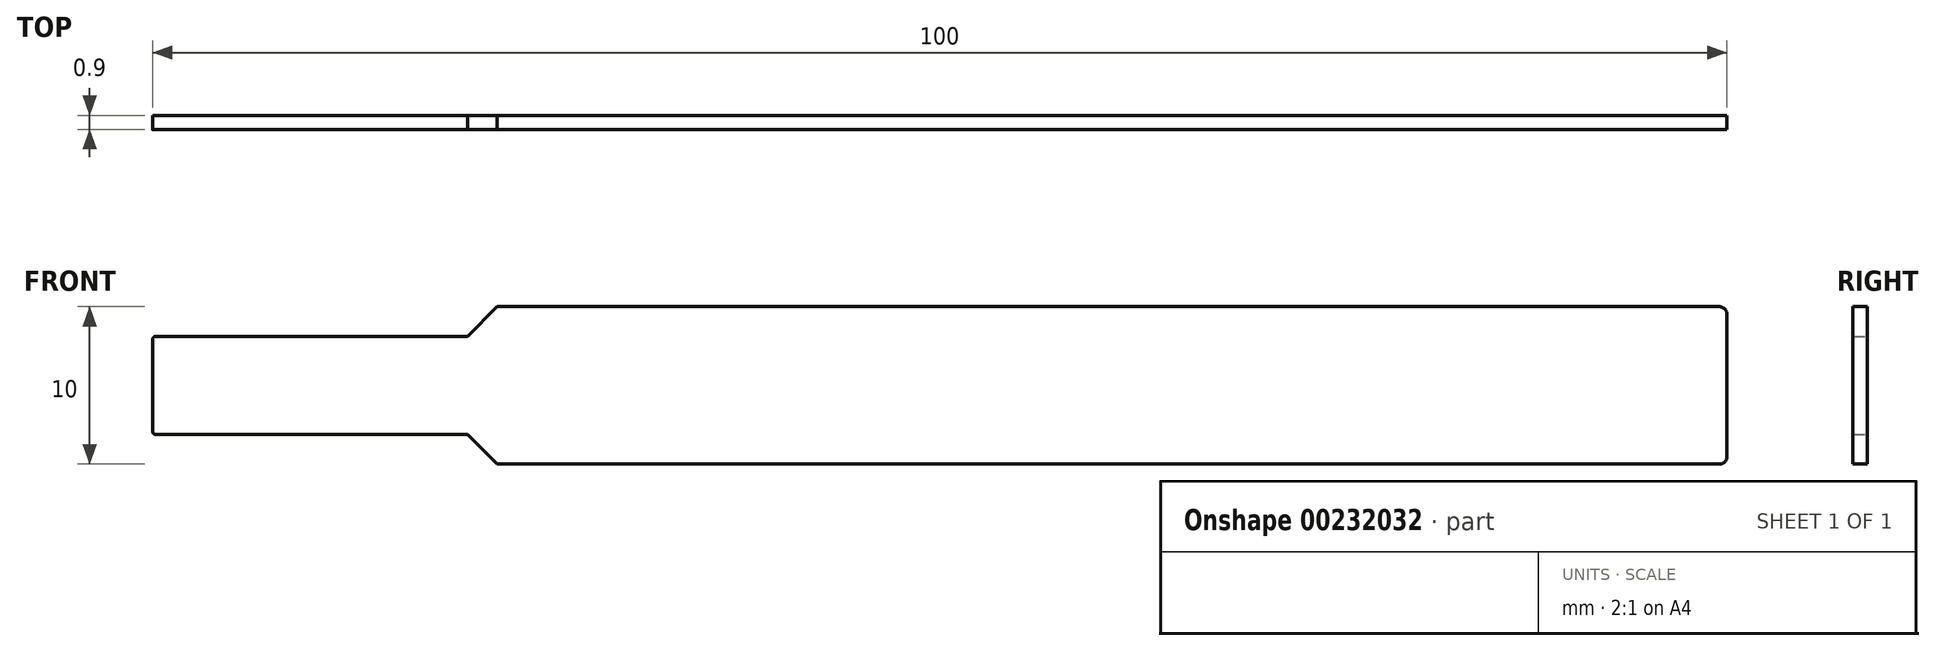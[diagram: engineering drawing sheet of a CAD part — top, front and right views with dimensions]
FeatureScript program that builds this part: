
annotation { "Feature Type Name" : "Feature", "Feature Type Description" : "" }
export const myFeature = defineFeature(function(context is Context, id is Id, definition is map)
    precondition{}
    {
        {
            var Q0;
            Q0=qCreatedBy(makeId("Front.planeOp"),FACE);
            var sketch = newSketch(context, id + "F0", { "sketchPlane" : qUnion([Q0])});
            skLineSegment(sketch, "E0", {"start": v(-20, 0) * mm, "end": v(-20, 3.12) * mm});
            skLineSegment(sketch, "E1", {"start": v(-20, 3.12) * mm, "end": v(0, 3.12) * mm});
            skLineSegment(sketch, "E2", {"start": v(1.88, 5) * mm, "end": v(80, 5) * mm});
            skLineSegment(sketch, "E3", {"start": v(80, 5) * mm, "end": v(80, 0) * mm});
            skLineSegment(sketch, "E4.MirrorCS", {"start": v(-20, 0) * mm, "end": v(-20, -3.12) * mm});
            skLineSegment(sketch, "E5.MirrorCS", {"start": v(-20, -3.12) * mm, "end": v(0, -3.12) * mm});
            skLineSegment(sketch, "E6.MirrorCS", {"start": v(1.88, -5) * mm, "end": v(80, -5) * mm});
            skLineSegment(sketch, "E7.MirrorCS", {"start": v(80, -5) * mm, "end": v(80, 0) * mm});
            skLineSegment(sketch, "E8", {"start": v(0, 3.12) * mm, "end": v(1.88, 5) * mm});
            skLineSegment(sketch, "E9.MirrorCS", {"start": v(0, -3.12) * mm, "end": v(1.88, -5) * mm});
            skPoint(sketch, "E10.orphan", {"position": v(0, 5) * mm});
            skPoint(sketch, "E11.MirrorCS.end.orphan", {"position": v(0, -5) * mm});
            skPoint(sketch, "E11.MirrorCS.start.orphan", {"position": v(0, -3.12) * mm});
            skSolve(sketch);
        }
        {
            var Q0;
            Q0=makeQuery(id+"F0.imprint","IMPRINT",FACE,{"disambiguationData":[TD([[makeQuery(id+"F0.imprint","IMPRINT",EDGE,{"derivedFrom":sQuery(id+"F0.wireOp",EDGE,"E0")}),-1.0]])]});
            extrude(context, id + "F1", {"entities" : qUnion([Q0]), "depth" : 0.9 * mm});
        }
        {
            var Q0;
            Q0=makeQuery(id+"F1.opExtrude","SWEPT_EDGE",EDGE,{"disambiguationData":[OSD([sQuery(id+"F0.wireOp",EDGE,"E4.MirrorCS"),sQuery(id+"F0.wireOp",EDGE,"E5.MirrorCS")])]});
            var Q1;
            Q1=makeQuery(id+"F1.opExtrude","SWEPT_EDGE",EDGE,{"disambiguationData":[OSD([sQuery(id+"F0.wireOp",EDGE,"E0"),sQuery(id+"F0.wireOp",EDGE,"E1")])]});
            fillet(context, id + "F2", {"entities" : qUnion([Q0, Q1]), "radius" : 0.2 * mm, "tangentPropagation" : true, "allowEdgeOverflow" : false});
        }
        {
            var Q0;
            Q0=makeQuery(id+"F1.opExtrude","SWEPT_EDGE",EDGE,{"disambiguationData":[OSD([sQuery(id+"F0.wireOp",EDGE,"E6.MirrorCS"),sQuery(id+"F0.wireOp",EDGE,"E7.MirrorCS")])]});
            var Q1;
            Q1=makeQuery(id+"F1.opExtrude","SWEPT_EDGE",EDGE,{"disambiguationData":[OSD([sQuery(id+"F0.wireOp",EDGE,"E2"),sQuery(id+"F0.wireOp",EDGE,"E3")])]});
            fillet(context, id + "F3", {"entities" : qUnion([Q0, Q1]), "radius" : 0.5 * mm, "tangentPropagation" : true, "allowEdgeOverflow" : false});
        }
    });
